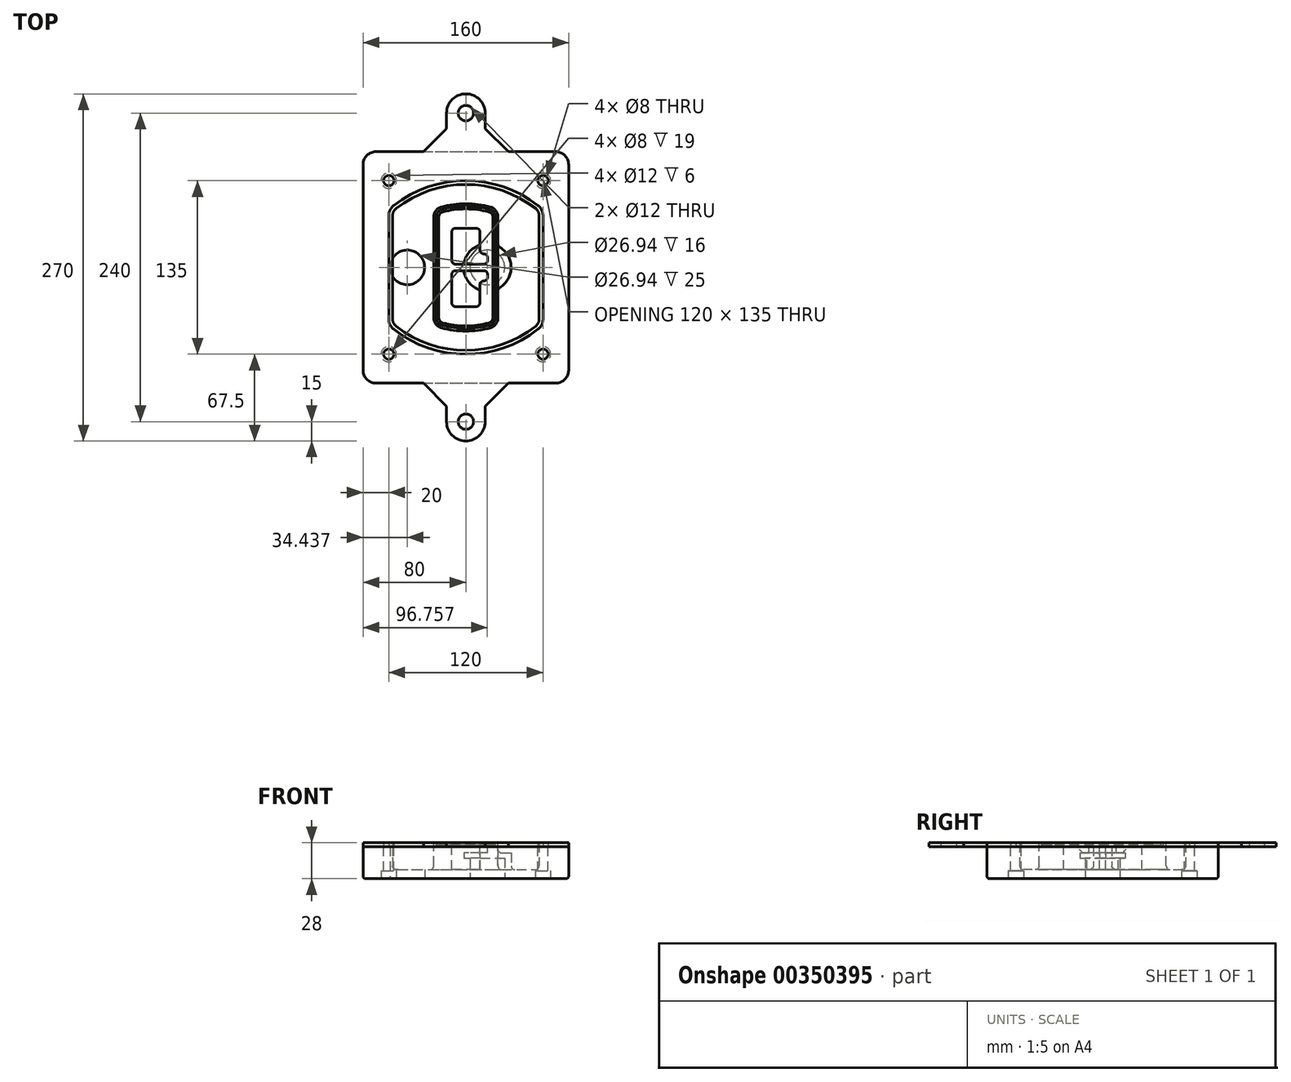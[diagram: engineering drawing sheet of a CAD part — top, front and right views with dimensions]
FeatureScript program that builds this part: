
annotation { "Feature Type Name" : "Feature", "Feature Type Description" : "" }
export const myFeature = defineFeature(function(context is Context, id is Id, definition is map)
    precondition{}
    {
        {
            var Q0;
            Q0=qCreatedBy(makeId("Top.planeOp"),FACE);
            var sketch = newSketch(context, id + "F0", { "sketchPlane" : qUnion([Q0])});
            skPoint(sketch, "E0.rect.middle", {"position": v(0, 0) * mm});
            skLineSegment(sketch, "E1.bottom", {"start": v(-70, -90) * mm, "end": v(70, -90) * mm});
            skLineSegment(sketch, "E1.top", {"start": v(-70, 90) * mm, "end": v(70, 90) * mm});
            skLineSegment(sketch, "E1.left", {"start": v(-80, -80) * mm, "end": v(-80, 80) * mm});
            skLineSegment(sketch, "E1.right", {"start": v(80, -80) * mm, "end": v(80, 80) * mm});
            skLineSegment(sketch, "E2", {"start": v(-80, 90) * mm, "end": v(80, -90) * mm, "construction": true});
            skLineSegment(sketch, "E3", {"start": v(80, 90) * mm, "end": v(-80, -90) * mm, "construction": true});
            skCircle(sketch, "E4", {"center": v(-60, 67.5) * mm, "radius": 4 * mm});
            skCircle(sketch, "E5", {"center": v(60, 67.5) * mm, "radius": 4 * mm});
            skCircle(sketch, "E6", {"center": v(60, -67.5) * mm, "radius": 4 * mm});
            skCircle(sketch, "E7", {"center": v(-60, -67.5) * mm, "radius": 4 * mm});
            skLineSegment(sketch, "E8", {"start": v(-60, 67.5) * mm, "end": v(60, 67.5) * mm, "construction": true});
            skLineSegment(sketch, "E9", {"start": v(60, 67.5) * mm, "end": v(60, -67.5) * mm, "construction": true});
            skLineSegment(sketch, "E10", {"start": v(60, -67.5) * mm, "end": v(-60, -67.5) * mm, "construction": true});
            skLineSegment(sketch, "E11", {"start": v(-60, -67.5) * mm, "end": v(-60, 67.5) * mm, "construction": true});
            skLineSegment(sketch, "E12", {"start": v(-60, 40.3) * mm, "end": v(-60, -40.3) * mm});
            skLineSegment(sketch, "E13", {"start": v(60, 40.3) * mm, "end": v(60, -40.3) * mm});
            skArc(sketch, "E14", {"start": v(56.15, 48.18) * mm, "mid": v(0, 67.5) * mm, "end": v(-56.15, 48.18) * mm});
            skArc(sketch, "E15", {"start": v(-56.15, -48.18) * mm, "mid": v(0, -67.5) * mm, "end": v(56.15, -48.18) * mm});
            skLineSegment(sketch, "E16", {"start": v(-60, 0) * mm, "end": v(60, 0) * mm, "construction": true});
            skPoint(sketch, "E17.visualSharp", {"position": v(-60, -45) * mm});
            skArc(sketch, "E17.filletArc", {"start": v(-60, -40.3) * mm, "mid": v(-58.99, -44.68) * mm, "end": v(-56.15, -48.18) * mm});
            skPoint(sketch, "E18.visualSharp", {"position": v(-60, 45) * mm});
            skArc(sketch, "E18.filletArc", {"start": v(-56.15, 48.18) * mm, "mid": v(-58.99, 44.68) * mm, "end": v(-60, 40.3) * mm});
            skPoint(sketch, "E19.visualSharp", {"position": v(60, 45) * mm});
            skArc(sketch, "E19.filletArc", {"start": v(60, 40.3) * mm, "mid": v(58.99, 44.68) * mm, "end": v(56.15, 48.18) * mm});
            skPoint(sketch, "E20.visualSharp", {"position": v(60, -45) * mm});
            skArc(sketch, "E20.filletArc", {"start": v(56.15, -48.18) * mm, "mid": v(58.99, -44.68) * mm, "end": v(60, -40.3) * mm});
            skPoint(sketch, "E21.visualSharp", {"position": v(-80, 90) * mm});
            skArc(sketch, "E21.filletArc", {"start": v(-70, 90) * mm, "mid": v(-77.07, 87.07) * mm, "end": v(-80, 80) * mm});
            skPoint(sketch, "E22.visualSharp", {"position": v(80, 90) * mm});
            skArc(sketch, "E22.filletArc", {"start": v(80, 80) * mm, "mid": v(77.07, 87.07) * mm, "end": v(70, 90) * mm});
            skPoint(sketch, "E23.visualSharp", {"position": v(80, -90) * mm});
            skArc(sketch, "E23.filletArc", {"start": v(70, -90) * mm, "mid": v(77.07, -87.07) * mm, "end": v(80, -80) * mm});
            skPoint(sketch, "E24.visualSharp", {"position": v(-80, -90) * mm});
            skArc(sketch, "E24.filletArc", {"start": v(-80, -80) * mm, "mid": v(-77.07, -87.07) * mm, "end": v(-70, -90) * mm});
            skArc(sketch, "E25.0", {"start": v(57, 40.3) * mm, "mid": v(56.3, 43.36) * mm, "end": v(54.3, 45.81) * mm});
            skLineSegment(sketch, "E25.1", {"start": v(57, 40.3) * mm, "end": v(57, -40.3) * mm});
            skArc(sketch, "E25.2", {"start": v(54.3, -45.81) * mm, "mid": v(56.3, -43.36) * mm, "end": v(57, -40.3) * mm});
            skArc(sketch, "E25.3", {"start": v(-54.3, -45.81) * mm, "mid": v(0, -64.5) * mm, "end": v(54.3, -45.81) * mm});
            skArc(sketch, "E25.4", {"start": v(-57, -40.3) * mm, "mid": v(-56.3, -43.36) * mm, "end": v(-54.3, -45.81) * mm});
            skArc(sketch, "E25.5", {"start": v(54.3, 45.81) * mm, "mid": v(0, 64.5) * mm, "end": v(-54.3, 45.81) * mm});
            skLineSegment(sketch, "E25.6", {"start": v(-57, 40.3) * mm, "end": v(-57, -40.3) * mm});
            skArc(sketch, "E25.7", {"start": v(-54.3, 45.81) * mm, "mid": v(-56.3, 43.36) * mm, "end": v(-57, 40.3) * mm});
            skArc(sketch, "E26.0", {"start": v(-58.62, 51.33) * mm, "mid": v(-62.58, 46.43) * mm, "end": v(-64, 40.3) * mm});
            skArc(sketch, "E26.1", {"start": v(58.62, 51.33) * mm, "mid": v(0, 71.5) * mm, "end": v(-58.62, 51.33) * mm});
            skArc(sketch, "E26.2", {"start": v(64, 40.3) * mm, "mid": v(62.58, 46.43) * mm, "end": v(58.62, 51.33) * mm});
            skLineSegment(sketch, "E26.3", {"start": v(64, 40.3) * mm, "end": v(64, -40.3) * mm});
            skArc(sketch, "E26.4", {"start": v(58.62, -51.33) * mm, "mid": v(62.58, -46.43) * mm, "end": v(64, -40.3) * mm});
            skLineSegment(sketch, "E26.5", {"start": v(-64, 40.3) * mm, "end": v(-64, -40.3) * mm});
            skArc(sketch, "E26.6", {"start": v(-58.62, -51.33) * mm, "mid": v(0, -71.5) * mm, "end": v(58.62, -51.33) * mm});
            skArc(sketch, "E26.7", {"start": v(-64, -40.3) * mm, "mid": v(-62.58, -46.43) * mm, "end": v(-58.62, -51.33) * mm});
            skSolve(sketch);
        }
        {
            var Q0;
            Q0=makeQuery(id+"F0.imprint","IMPRINT",FACE,{"disambiguationData":[TD([[makeQuery(id+"F0.imprint","IMPRINT",EDGE,{"derivedFrom":sQuery(id+"F0.wireOp",EDGE,"E1.bottom")}),1.0]])]});
            var Q1;
            Q1=makeQuery(id+"F0.imprint","IMPRINT",FACE,{"disambiguationData":[TD([[makeQuery(id+"F0.imprint","IMPRINT",EDGE,{"derivedFrom":sQuery(id+"F0.wireOp",EDGE,"E12")}),1.0]])]});
            var Q2;
            Q2=makeQuery(id+"F0.imprint","IMPRINT",FACE,{"disambiguationData":[TD([[makeQuery(id+"F0.imprint","IMPRINT",EDGE,{"derivedFrom":sQuery(id+"F0.wireOp",EDGE,"E25.0")}),1.0]])]});
            var Q3;
            Q3=makeQuery(id+"F0.imprint","IMPRINT",FACE,{"disambiguationData":[TD([[makeQuery(id+"F0.imprint","IMPRINT",EDGE,{"derivedFrom":sQuery(id+"F0.wireOp",EDGE,"E12")}),-1.0]])]});
            extrude(context, id + "F1", {"entities" : qUnion([Q0, Q1, Q2, Q3]), "oppositeDirection" : true, "depth" : 25 * mm});
        }
        {
            var Q0;
            Q0=makeQuery(id+"F0.imprint","IMPRINT",FACE,{"disambiguationData":[TD([[makeQuery(id+"F0.imprint","IMPRINT",EDGE,{"derivedFrom":sQuery(id+"F0.wireOp",EDGE,"E12")}),1.0]])]});
            extrude(context, id + "F2", {"entities" : qUnion([Q0]), "operationType" : NewBodyOperationType.ADD, "depth" : 3 * mm});
        }
        {
            var Q0;
            Q0=makeQuery(id+"F0.imprint","IMPRINT",FACE,{"disambiguationData":[TD([[makeQuery(id+"F0.imprint","IMPRINT",EDGE,{"derivedFrom":sQuery(id+"F0.wireOp",EDGE,"E25.0")}),1.0]])]});
            extrude(context, id + "F3", {"entities" : qUnion([Q0]), "operationType" : NewBodyOperationType.REMOVE, "oppositeDirection" : true, "depth" : 18 * mm});
        }
        {
            var Q0;
            Q0=makeQuery(id+"F2.opExtrude","CAP_FACE",FACE,{"disambiguationData":[OSD([sQuery(id+"F0.wireOp",EDGE,"E12"),sQuery(id+"F0.wireOp",EDGE,"E13"),sQuery(id+"F0.wireOp",EDGE,"E14"),sQuery(id+"F0.wireOp",EDGE,"E15"),sQuery(id+"F0.wireOp",EDGE,"E17.filletArc"),sQuery(id+"F0.wireOp",EDGE,"E18.filletArc"),sQuery(id+"F0.wireOp",EDGE,"E19.filletArc"),sQuery(id+"F0.wireOp",EDGE,"E20.filletArc"),sQuery(id+"F0.wireOp",EDGE,"E25.0"),sQuery(id+"F0.wireOp",EDGE,"E25.1"),sQuery(id+"F0.wireOp",EDGE,"E25.2"),sQuery(id+"F0.wireOp",EDGE,"E25.3"),sQuery(id+"F0.wireOp",EDGE,"E25.4"),sQuery(id+"F0.wireOp",EDGE,"E25.5"),sQuery(id+"F0.wireOp",EDGE,"E25.6"),sQuery(id+"F0.wireOp",EDGE,"E25.7")])],"isStart":false});
            var sketch = newSketch(context, id + "F4", { "sketchPlane" : qUnion([Q0])});
            skArc(sketch, "E27.0", {"start": v(-19.08, -46.97) * mm, "mid": v(0, -49.5) * mm, "end": v(19.08, -46.97) * mm});
            skArc(sketch, "E28.0", {"start": v(19.08, 46.97) * mm, "mid": v(0, 49.5) * mm, "end": v(-19.08, 46.97) * mm});
            skLineSegment(sketch, "E29", {"start": v(-25, 39.25) * mm, "end": v(-25, -39.25) * mm});
            skLineSegment(sketch, "E30", {"start": v(25, 39.25) * mm, "end": v(25, -39.25) * mm});
            skLineSegment(sketch, "E31", {"start": v(-25, 45.1) * mm, "end": v(25, 45.1) * mm, "construction": true});
            skLineSegment(sketch, "E32", {"start": v(-25, -45.1) * mm, "end": v(25, -45.1) * mm, "construction": true});
            skPoint(sketch, "E33.visualSharp", {"position": v(-25, 45.1) * mm});
            skArc(sketch, "E33.filletArc", {"start": v(-19.08, 46.97) * mm, "mid": v(-23.35, 44.11) * mm, "end": v(-25, 39.25) * mm});
            skPoint(sketch, "E34.visualSharp", {"position": v(25, 45.1) * mm});
            skArc(sketch, "E34.filletArc", {"start": v(25, 39.25) * mm, "mid": v(23.35, 44.11) * mm, "end": v(19.08, 46.97) * mm});
            skPoint(sketch, "E35.visualSharp", {"position": v(25, -45.1) * mm});
            skArc(sketch, "E35.filletArc", {"start": v(19.08, -46.97) * mm, "mid": v(23.35, -44.11) * mm, "end": v(25, -39.25) * mm});
            skPoint(sketch, "E36.visualSharp", {"position": v(-25, -45.1) * mm});
            skArc(sketch, "E36.filletArc", {"start": v(-25, -39.25) * mm, "mid": v(-23.35, -44.11) * mm, "end": v(-19.08, -46.97) * mm});
            skArc(sketch, "E37.0", {"start": v(54.3, 45.81) * mm, "mid": v(0, 64.5) * mm, "end": v(-54.3, 45.81) * mm});
            skArc(sketch, "E37.1", {"start": v(-54.3, 45.81) * mm, "mid": v(-56.3, 43.36) * mm, "end": v(-57, 40.3) * mm});
            skLineSegment(sketch, "E37.2", {"start": v(-57, 40.3) * mm, "end": v(-57, -40.3) * mm});
            skArc(sketch, "E37.3", {"start": v(-57, -40.3) * mm, "mid": v(-56.3, -43.36) * mm, "end": v(-54.3, -45.81) * mm});
            skArc(sketch, "E37.4", {"start": v(-54.3, -45.81) * mm, "mid": v(0, -64.5) * mm, "end": v(54.3, -45.81) * mm});
            skArc(sketch, "E37.5", {"start": v(54.3, -45.81) * mm, "mid": v(56.3, -43.36) * mm, "end": v(57, -40.3) * mm});
            skLineSegment(sketch, "E37.6", {"start": v(57, 40.3) * mm, "end": v(57, -40.3) * mm});
            skArc(sketch, "E37.7", {"start": v(57, 40.3) * mm, "mid": v(56.3, 43.36) * mm, "end": v(54.3, 45.81) * mm});
            skLineSegment(sketch, "E38.0", {"start": v(23, 39.25) * mm, "end": v(23, -39.25) * mm});
            skArc(sketch, "E38.1", {"start": v(18.56, -45.04) * mm, "mid": v(21.76, -42.9) * mm, "end": v(23, -39.25) * mm});
            skArc(sketch, "E38.2", {"start": v(-18.56, -45.04) * mm, "mid": v(0, -47.5) * mm, "end": v(18.56, -45.04) * mm});
            skArc(sketch, "E38.3", {"start": v(-23, -39.25) * mm, "mid": v(-21.76, -42.9) * mm, "end": v(-18.56, -45.04) * mm});
            skLineSegment(sketch, "E38.4", {"start": v(-23, 39.25) * mm, "end": v(-23, -39.25) * mm});
            skArc(sketch, "E38.5", {"start": v(23, 39.25) * mm, "mid": v(21.76, 42.9) * mm, "end": v(18.56, 45.04) * mm});
            skArc(sketch, "E38.6", {"start": v(-18.56, 45.04) * mm, "mid": v(-21.76, 42.9) * mm, "end": v(-23, 39.25) * mm});
            skArc(sketch, "E38.7", {"start": v(18.56, 45.04) * mm, "mid": v(0, 47.5) * mm, "end": v(-18.56, 45.04) * mm});
            skArc(sketch, "E39.0", {"start": v(21, 39.25) * mm, "mid": v(20.18, 41.68) * mm, "end": v(18.04, 43.1) * mm});
            skLineSegment(sketch, "E39.1", {"start": v(21, 39.25) * mm, "end": v(21, -39.25) * mm});
            skArc(sketch, "E39.2", {"start": v(18.04, -43.1) * mm, "mid": v(20.18, -41.68) * mm, "end": v(21, -39.25) * mm});
            skArc(sketch, "E39.3", {"start": v(-18.04, -43.1) * mm, "mid": v(0, -45.5) * mm, "end": v(18.04, -43.1) * mm});
            skArc(sketch, "E39.4", {"start": v(-21, -39.25) * mm, "mid": v(-20.18, -41.68) * mm, "end": v(-18.04, -43.1) * mm});
            skArc(sketch, "E39.5", {"start": v(18.04, 43.1) * mm, "mid": v(0, 45.5) * mm, "end": v(-18.04, 43.1) * mm});
            skLineSegment(sketch, "E39.6", {"start": v(-21, 39.25) * mm, "end": v(-21, -39.25) * mm});
            skArc(sketch, "E39.7", {"start": v(-18.04, 43.1) * mm, "mid": v(-20.18, 41.68) * mm, "end": v(-21, 39.25) * mm});
            skLineSegment(sketch, "E40", {"start": v(-25, 0) * mm, "end": v(25, 0) * mm, "construction": true});
            skLineSegment(sketch, "E41", {"start": v(-11, 5.5) * mm, "end": v(-11, 27.5) * mm});
            skLineSegment(sketch, "E42", {"start": v(-8, 30.5) * mm, "end": v(8, 30.5) * mm});
            skLineSegment(sketch, "E43", {"start": v(11, 27.5) * mm, "end": v(11, 13.5) * mm});
            skLineSegment(sketch, "E44", {"start": v(14, 10.5) * mm, "end": v(14, 10.5) * mm});
            skLineSegment(sketch, "E45", {"start": v(17, 7.5) * mm, "end": v(17, 5.5) * mm});
            skLineSegment(sketch, "E46", {"start": v(14, 2.5) * mm, "end": v(-8, 2.5) * mm});
            skPoint(sketch, "E47.visualSharp", {"position": v(-11, 30.5) * mm});
            skArc(sketch, "E47.filletArc", {"start": v(-8, 30.5) * mm, "mid": v(-10.12, 29.62) * mm, "end": v(-11, 27.5) * mm});
            skPoint(sketch, "E48.visualSharp", {"position": v(11, 30.5) * mm});
            skArc(sketch, "E48.filletArc", {"start": v(11, 27.5) * mm, "mid": v(10.12, 29.62) * mm, "end": v(8, 30.5) * mm});
            skPoint(sketch, "E49.visualSharp", {"position": v(11, 10.5) * mm});
            skArc(sketch, "E49.filletArc", {"start": v(11, 13.5) * mm, "mid": v(11.88, 11.38) * mm, "end": v(14, 10.5) * mm});
            skPoint(sketch, "E50.visualSharp", {"position": v(17, 10.5) * mm});
            skArc(sketch, "E50.filletArc", {"start": v(17, 7.5) * mm, "mid": v(16.12, 9.62) * mm, "end": v(14, 10.5) * mm});
            skPoint(sketch, "E51.visualSharp", {"position": v(17, 2.5) * mm});
            skArc(sketch, "E51.filletArc", {"start": v(14, 2.5) * mm, "mid": v(16.12, 3.38) * mm, "end": v(17, 5.5) * mm});
            skPoint(sketch, "E52.visualSharp", {"position": v(-11, 2.5) * mm});
            skArc(sketch, "E52.filletArc", {"start": v(-11, 5.5) * mm, "mid": v(-10.12, 3.38) * mm, "end": v(-8, 2.5) * mm});
            skLineSegment(sketch, "E53.0.MirrorCS", {"start": v(14, -2.5) * mm, "end": v(-8, -2.5) * mm});
            skArc(sketch, "E54.0.MirrorCS", {"start": v(-11, -5.5) * mm, "mid": v(-10.12, -3.38) * mm, "end": v(-8, -2.5) * mm});
            skLineSegment(sketch, "E55.0.MirrorCS", {"start": v(-11, -5.5) * mm, "end": v(-11, -27.5) * mm});
            skArc(sketch, "E56.0.MirrorCS", {"start": v(-8, -30.5) * mm, "mid": v(-10.12, -29.62) * mm, "end": v(-11, -27.5) * mm});
            skLineSegment(sketch, "E57.0.MirrorCS", {"start": v(-8, -30.5) * mm, "end": v(8, -30.5) * mm});
            skArc(sketch, "E58.0.MirrorCS", {"start": v(11, -27.5) * mm, "mid": v(10.12, -29.62) * mm, "end": v(8, -30.5) * mm});
            skLineSegment(sketch, "E59.0.MirrorCS", {"start": v(11, -27.5) * mm, "end": v(11, -13.5) * mm});
            skArc(sketch, "E60.0.MirrorCS", {"start": v(11, -13.5) * mm, "mid": v(11.88, -11.38) * mm, "end": v(14, -10.5) * mm});
            skArc(sketch, "E61.0.MirrorCS", {"start": v(17, -7.5) * mm, "mid": v(16.12, -9.62) * mm, "end": v(14, -10.5) * mm});
            skLineSegment(sketch, "E62.0.MirrorCS", {"start": v(17, -7.5) * mm, "end": v(17, -5.5) * mm});
            skArc(sketch, "E63.0.MirrorCS", {"start": v(14, -2.5) * mm, "mid": v(16.12, -3.38) * mm, "end": v(17, -5.5) * mm});
            skSolve(sketch);
        }
        {
            var Q0;
            Q0=makeQuery(id+"F4.imprint","IMPRINT",FACE,{"disambiguationData":[TD([[makeQuery(id+"F4.imprint","IMPRINT",EDGE,{"derivedFrom":sQuery(id+"F4.wireOp",EDGE,"E27.0")}),1.0]])]});
            var Q1;
            Q1=makeQuery(id+"F4.imprint","IMPRINT",FACE,{"disambiguationData":[TD([[makeQuery(id+"F4.imprint","IMPRINT",EDGE,{"derivedFrom":sQuery(id+"F4.wireOp",EDGE,"E38.0")}),-1.0]])]});
            var Q2;
            Q2=makeQuery(id+"F4.imprint","IMPRINT",FACE,{"disambiguationData":[TD([[makeQuery(id+"F4.imprint","IMPRINT",EDGE,{"derivedFrom":sQuery(id+"F4.wireOp",EDGE,"E39.0")}),1.0]])]});
            extrude(context, id + "F5", {"entities" : qUnion([Q0, Q1, Q2]), "operationType" : NewBodyOperationType.ADD, "endBound" : BoundingType.UP_TO_NEXT, "oppositeDirection" : true, "depth" : 25 * mm});
        }
        {
            var Q0;
            Q0=makeQuery(id+"F4.imprint","IMPRINT",FACE,{"disambiguationData":[TD([[makeQuery(id+"F4.imprint","IMPRINT",EDGE,{"derivedFrom":sQuery(id+"F4.wireOp",EDGE,"E38.0")}),-1.0]])]});
            extrude(context, id + "F6", {"entities" : qUnion([Q0]), "operationType" : NewBodyOperationType.REMOVE, "oppositeDirection" : true, "depth" : 2 * mm});
        }
        {
            var Q0;
            Q0=makeQuery(id+"F1.opExtrude","CAP_FACE",FACE,{"disambiguationData":[OSD([sQuery(id+"F0.wireOp",EDGE,"E1.bottom"),sQuery(id+"F0.wireOp",EDGE,"E1.top"),sQuery(id+"F0.wireOp",EDGE,"E1.left"),sQuery(id+"F0.wireOp",EDGE,"E1.right"),sQuery(id+"F0.wireOp",EDGE,"E4"),sQuery(id+"F0.wireOp",EDGE,"E5"),sQuery(id+"F0.wireOp",EDGE,"E6"),sQuery(id+"F0.wireOp",EDGE,"E7"),sQuery(id+"F0.wireOp",EDGE,"E21.filletArc"),sQuery(id+"F0.wireOp",EDGE,"E22.filletArc"),sQuery(id+"F0.wireOp",EDGE,"E23.filletArc"),sQuery(id+"F0.wireOp",EDGE,"E24.filletArc")])],"isStart":false});
            var sketch = newSketch(context, id + "F7", { "sketchPlane" : qUnion([Q0])});
            skCircle(sketch, "E64", {"center": v(16.76, 0) * mm, "radius": 13.47 * mm});
            skCircle(sketch, "E65", {"center": v(-45.56, 0) * mm, "radius": 13.47 * mm});
            skLineSegment(sketch, "E66", {"start": v(80, 0) * mm, "end": v(-80, 0) * mm});
            skCircle(sketch, "E67", {"center": v(16.76, 0) * mm, "radius": 18.47 * mm});
            skCircle(sketch, "E68", {"center": v(60, -67.5) * mm, "radius": 6 * mm});
            skCircle(sketch, "E69", {"center": v(-60, -67.5) * mm, "radius": 6 * mm});
            skCircle(sketch, "E70", {"center": v(-60, 67.5) * mm, "radius": 6 * mm});
            skCircle(sketch, "E71", {"center": v(60, 67.5) * mm, "radius": 6 * mm});
            skSolve(sketch);
        }
        {
            var Q0;
            {var subQ1=sQuery(id+"F7.wireOp",EDGE,"E66");var subQ4=sQuery(id+"F7.wireOp",EDGE,"E64");var subQ6=makeQuery(id+"F7.imprint","INTERSECT",VERTEX,{"disambiguationData":[OD(0.0)],"derivedFrom":[subQ4,subQ1]});Q0=makeQuery(id+"F7.imprint","IMPRINT",FACE,{"disambiguationData":[TD([[makeQuery(id+"F7.imprint","IMPRINT",EDGE,{"disambiguationData":[TD([[subQ6,-1.0]])],"derivedFrom":subQ4}),-1.0]])]});}
            var Q1;
            {var subQ0=sQuery(id+"F7.wireOp",EDGE,"E66");var subQ1=sQuery(id+"F7.wireOp",EDGE,"E64");var subQ3=makeQuery(id+"F7.imprint","INTERSECT",VERTEX,{"disambiguationData":[OD(0.0)],"derivedFrom":[subQ1,subQ0]});Q1=makeQuery(id+"F7.imprint","IMPRINT",FACE,{"disambiguationData":[TD([[makeQuery(id+"F7.imprint","IMPRINT",EDGE,{"disambiguationData":[TD([[subQ3,-1.0]])],"derivedFrom":subQ1}),1.0]])]});}
            var Q2;
            {var subQ0=sQuery(id+"F7.wireOp",EDGE,"E66");var subQ1=sQuery(id+"F7.wireOp",EDGE,"E64");var subQ3=makeQuery(id+"F7.imprint","INTERSECT",VERTEX,{"disambiguationData":[OD(0.0)],"derivedFrom":[subQ1,subQ0]});Q2=makeQuery(id+"F7.imprint","IMPRINT",FACE,{"disambiguationData":[TD([[makeQuery(id+"F7.imprint","IMPRINT",EDGE,{"disambiguationData":[TD([[subQ3,1.0]])],"derivedFrom":subQ1}),1.0]])]});}
            var Q3;
            {var subQ1=sQuery(id+"F7.wireOp",EDGE,"E66");var subQ4=sQuery(id+"F7.wireOp",EDGE,"E64");var subQ6=makeQuery(id+"F7.imprint","INTERSECT",VERTEX,{"disambiguationData":[OD(0.0)],"derivedFrom":[subQ4,subQ1]});Q3=makeQuery(id+"F7.imprint","IMPRINT",FACE,{"disambiguationData":[TD([[makeQuery(id+"F7.imprint","IMPRINT",EDGE,{"disambiguationData":[TD([[subQ6,1.0]])],"derivedFrom":subQ4}),-1.0]])]});}
            extrude(context, id + "F8", {"entities" : qUnion([Q0, Q1, Q2, Q3]), "operationType" : NewBodyOperationType.ADD, "oppositeDirection" : true, "depth" : 20 * mm});
        }
        {
            var Q0;
            {var subQ0=sQuery(id+"F7.wireOp",EDGE,"E66");var subQ1=sQuery(id+"F7.wireOp",EDGE,"E64");var subQ3=makeQuery(id+"F7.imprint","INTERSECT",VERTEX,{"disambiguationData":[OD(0.0)],"derivedFrom":[subQ1,subQ0]});Q0=makeQuery(id+"F7.imprint","IMPRINT",FACE,{"disambiguationData":[TD([[makeQuery(id+"F7.imprint","IMPRINT",EDGE,{"disambiguationData":[TD([[subQ3,-1.0]])],"derivedFrom":subQ1}),1.0]])]});}
            var Q1;
            {var subQ0=sQuery(id+"F7.wireOp",EDGE,"E66");var subQ1=sQuery(id+"F7.wireOp",EDGE,"E64");var subQ3=makeQuery(id+"F7.imprint","INTERSECT",VERTEX,{"disambiguationData":[OD(0.0)],"derivedFrom":[subQ1,subQ0]});Q1=makeQuery(id+"F7.imprint","IMPRINT",FACE,{"disambiguationData":[TD([[makeQuery(id+"F7.imprint","IMPRINT",EDGE,{"disambiguationData":[TD([[subQ3,1.0]])],"derivedFrom":subQ1}),1.0]])]});}
            extrude(context, id + "F9", {"entities" : qUnion([Q0, Q1]), "operationType" : NewBodyOperationType.REMOVE, "oppositeDirection" : true, "depth" : 16 * mm});
        }
        {
            var Q0;
            {var subQ0=sQuery(id+"F7.wireOp",EDGE,"E66");var subQ1=sQuery(id+"F7.wireOp",EDGE,"E65");var subQ3=makeQuery(id+"F7.imprint","INTERSECT",VERTEX,{"disambiguationData":[OD(0.0)],"derivedFrom":[subQ1,subQ0]});Q0=makeQuery(id+"F7.imprint","IMPRINT",FACE,{"disambiguationData":[TD([[makeQuery(id+"F7.imprint","IMPRINT",EDGE,{"disambiguationData":[TD([[subQ3,-1.0]])],"derivedFrom":subQ1}),1.0]])]});}
            var Q1;
            {var subQ0=sQuery(id+"F7.wireOp",EDGE,"E66");var subQ1=sQuery(id+"F7.wireOp",EDGE,"E65");var subQ3=makeQuery(id+"F7.imprint","INTERSECT",VERTEX,{"disambiguationData":[OD(0.0)],"derivedFrom":[subQ1,subQ0]});Q1=makeQuery(id+"F7.imprint","IMPRINT",FACE,{"disambiguationData":[TD([[makeQuery(id+"F7.imprint","IMPRINT",EDGE,{"disambiguationData":[TD([[subQ3,1.0]])],"derivedFrom":subQ1}),1.0]])]});}
            extrude(context, id + "F10", {"entities" : qUnion([Q0, Q1]), "operationType" : NewBodyOperationType.REMOVE, "oppositeDirection" : true, "depth" : 25 * mm});
        }
        {
            var Q0;
            Q0=makeQuery(id+"F7.imprint","IMPRINT",FACE,{"disambiguationData":[TD([[makeQuery(id+"F7.imprint","IMPRINT",EDGE,{"derivedFrom":sQuery(id+"F7.wireOp",EDGE,"E68")}),1.0]])]});
            var Q1;
            Q1=makeQuery(id+"F7.imprint","IMPRINT",FACE,{"disambiguationData":[TD([[makeQuery(id+"F7.imprint","IMPRINT",EDGE,{"derivedFrom":makeQuery(id+"F1.opExtrude","CAP_EDGE",EDGE,{"disambiguationData":[OSD([sQuery(id+"F0.wireOp",EDGE,"E5")])],"isStart":false})}),-1.0]])]});
            var Q2;
            Q2=makeQuery(id+"F7.imprint","IMPRINT",FACE,{"disambiguationData":[TD([[makeQuery(id+"F7.imprint","IMPRINT",EDGE,{"derivedFrom":sQuery(id+"F7.wireOp",EDGE,"E69")}),1.0]])]});
            var Q3;
            Q3=makeQuery(id+"F7.imprint","IMPRINT",FACE,{"disambiguationData":[TD([[makeQuery(id+"F7.imprint","IMPRINT",EDGE,{"derivedFrom":makeQuery(id+"F1.opExtrude","CAP_EDGE",EDGE,{"disambiguationData":[OSD([sQuery(id+"F0.wireOp",EDGE,"E4")])],"isStart":false})}),-1.0]])]});
            var Q4;
            Q4=makeQuery(id+"F7.imprint","IMPRINT",FACE,{"disambiguationData":[TD([[makeQuery(id+"F7.imprint","IMPRINT",EDGE,{"derivedFrom":sQuery(id+"F7.wireOp",EDGE,"E70")}),1.0]])]});
            var Q5;
            Q5=makeQuery(id+"F7.imprint","IMPRINT",FACE,{"disambiguationData":[TD([[makeQuery(id+"F7.imprint","IMPRINT",EDGE,{"derivedFrom":makeQuery(id+"F1.opExtrude","CAP_EDGE",EDGE,{"disambiguationData":[OSD([sQuery(id+"F0.wireOp",EDGE,"E7")])],"isStart":false})}),-1.0]])]});
            var Q6;
            Q6=makeQuery(id+"F7.imprint","IMPRINT",FACE,{"disambiguationData":[TD([[makeQuery(id+"F7.imprint","IMPRINT",EDGE,{"derivedFrom":sQuery(id+"F7.wireOp",EDGE,"E71")}),1.0]])]});
            var Q7;
            Q7=makeQuery(id+"F7.imprint","IMPRINT",FACE,{"disambiguationData":[TD([[makeQuery(id+"F7.imprint","IMPRINT",EDGE,{"derivedFrom":makeQuery(id+"F1.opExtrude","CAP_EDGE",EDGE,{"disambiguationData":[OSD([sQuery(id+"F0.wireOp",EDGE,"E6")])],"isStart":false})}),-1.0]])]});
            extrude(context, id + "F11", {"entities" : qUnion([Q0, Q1, Q2, Q3, Q4, Q5, Q6, Q7]), "operationType" : NewBodyOperationType.REMOVE, "oppositeDirection" : true, "depth" : 6 * mm});
        }
        {
            var Q0;
            Q0=makeQuery(id+"F9.boolean.opBoolean","COPY",FACE,{"derivedFrom":makeQuery(id+"F9.opExtrude","CAP_FACE",FACE,{"disambiguationData":[OSD([sQuery(id+"F7.wireOp",EDGE,"E64")])],"isStart":false})});
            var sketch = newSketch(context, id + "F12", { "sketchPlane" : qUnion([Q0])});
            skArc(sketch, "E72.0", {"start": v(11, 17.55) * mm, "mid": v(2.57, 11.82) * mm, "end": v(-1.54, 2.5) * mm});
            skArc(sketch, "E72.1", {"start": v(-1.54, -2.5) * mm, "mid": v(2.57, -11.82) * mm, "end": v(11, -17.55) * mm});
            skLineSegment(sketch, "E73", {"start": v(-1.54, -2.5) * mm, "end": v(14, -2.5) * mm});
            skLineSegment(sketch, "E74.0", {"start": v(14, 2.5) * mm, "end": v(-1.54, 2.5) * mm});
            skArc(sketch, "E74.1", {"start": v(14, 2.5) * mm, "mid": v(16.12, 3.38) * mm, "end": v(17, 5.5) * mm});
            skLineSegment(sketch, "E74.2", {"start": v(17, 7.5) * mm, "end": v(17, 5.5) * mm});
            skArc(sketch, "E74.3", {"start": v(17, 7.5) * mm, "mid": v(16.12, 9.62) * mm, "end": v(14, 10.5) * mm});
            skArc(sketch, "E74.4", {"start": v(11, 13.5) * mm, "mid": v(11.88, 11.38) * mm, "end": v(14, 10.5) * mm});
            skLineSegment(sketch, "E74.5", {"start": v(11, 17.55) * mm, "end": v(11, 13.5) * mm});
            skLineSegment(sketch, "E74.7", {"start": v(14, -2.5) * mm, "end": v(-1.54, -2.5) * mm});
            skArc(sketch, "E74.8", {"start": v(14, -2.5) * mm, "mid": v(16.12, -3.38) * mm, "end": v(17, -5.5) * mm});
            skLineSegment(sketch, "E74.9", {"start": v(17, -7.5) * mm, "end": v(17, -5.5) * mm});
            skArc(sketch, "E74.10", {"start": v(17, -7.5) * mm, "mid": v(16.12, -9.62) * mm, "end": v(14, -10.5) * mm});
            skArc(sketch, "E74.11", {"start": v(11, -13.5) * mm, "mid": v(11.88, -11.38) * mm, "end": v(14, -10.5) * mm});
            skLineSegment(sketch, "E74.12", {"start": v(11, -17.55) * mm, "end": v(11, -13.5) * mm});
            skPoint(sketch, "E75.orphan", {"position": v(11, -27.5) * mm});
            skPoint(sketch, "E76.orphan", {"position": v(-8, -2.5) * mm});
            skPoint(sketch, "E77.orphan", {"position": v(-8, 2.5) * mm});
            skPoint(sketch, "E78.orphan", {"position": v(11, 27.5) * mm});
            skSolve(sketch);
        }
        {
            var Q0;
            {var subQ7=sQuery(id+"F12.wireOp",EDGE,"E72.0");var subQ14=sQuery(id+"F12.wireOp",EDGE,"E72.1");var subQ16=sQuery(id+"F12.wireOp",EDGE,"E74.1");var subQ18=sQuery(id+"F12.wireOp",EDGE,"E74.8");Q0=qUnion([makeQuery(id+"F12.imprint","IMPRINT",FACE,{"disambiguationData":[TD([[makeQuery(id+"F12.imprint","IMPRINT",EDGE,{"derivedFrom":subQ7}),1.0]])]}),makeQuery(id+"F12.imprint","IMPRINT",FACE,{"disambiguationData":[TD([[makeQuery(id+"F12.imprint","IMPRINT",EDGE,{"derivedFrom":subQ14}),1.0]])]}),makeQuery(id+"F12.imprint","IMPRINT",FACE,{"disambiguationData":[TD([[makeQuery(id+"F12.imprint","IMPRINT",EDGE,{"derivedFrom":subQ16}),1.0]])]}),makeQuery(id+"F12.imprint","IMPRINT",FACE,{"disambiguationData":[TD([[makeQuery(id+"F12.imprint","IMPRINT",EDGE,{"derivedFrom":subQ18}),-1.0]])]})]);}
            var Q1;
            Q1=makeQuery(id+"F5.boolean.opBoolean","SPLIT",FACE,{"disambiguationData":[TD([makeQuery(id+"F5.opExtrude","SWEPT_FACE",FACE,{"disambiguationData":[OSD([sQuery(id+"F4.wireOp",EDGE,"E41")])]})])],"derivedFrom":makeQuery(id+"F3.boolean.opBoolean","COPY",FACE,{"derivedFrom":makeQuery(id+"F3.opExtrude","CAP_FACE",FACE,{"disambiguationData":[OSD([sQuery(id+"F0.wireOp",EDGE,"E25.0"),sQuery(id+"F0.wireOp",EDGE,"E25.1"),sQuery(id+"F0.wireOp",EDGE,"E25.2"),sQuery(id+"F0.wireOp",EDGE,"E25.3"),sQuery(id+"F0.wireOp",EDGE,"E25.4"),sQuery(id+"F0.wireOp",EDGE,"E25.5"),sQuery(id+"F0.wireOp",EDGE,"E25.6"),sQuery(id+"F0.wireOp",EDGE,"E25.7")])],"isStart":false})})});
            extrude(context, id + "F13", {"entities" : qUnion([Q0]), "operationType" : NewBodyOperationType.REMOVE, "endBound" : BoundingType.UP_TO_SURFACE, "endBoundEntityFace" : qUnion([Q1]), "depth" : 25 * mm});
        }
        {
            var Q0;
            Q0=makeQuery(id+"F3.boolean.opBoolean","COPY",EDGE,{"derivedFrom":makeQuery(id+"F3.opExtrude","CAP_EDGE",EDGE,{"disambiguationData":[OSD([sQuery(id+"F0.wireOp",EDGE,"E25.6")])],"isStart":false})});
            var Q1;
            Q1=makeQuery(id+"F8.boolean.opBoolean","INTERSECT",EDGE,{"derivedFrom":[makeQuery(id+"F5.opExtrude","SWEPT_FACE",FACE,{"disambiguationData":[OSD([sQuery(id+"F4.wireOp",EDGE,"E30")])]}),makeQuery(id+"F8.opExtrude","CAP_FACE",FACE,{"disambiguationData":[OSD([sQuery(id+"F7.wireOp",EDGE,"E67")])],"isStart":false})]});
            var Q2;
            Q2=makeQuery(id+"F8.boolean.opBoolean","INTERSECT",EDGE,{"disambiguationData":[OD(1.0)],"derivedFrom":[makeQuery(id+"F5.opExtrude","SWEPT_FACE",FACE,{"disambiguationData":[OSD([sQuery(id+"F4.wireOp",EDGE,"E30")])]}),makeQuery(id+"F8.opExtrude","SWEPT_FACE",FACE,{"disambiguationData":[OSD([sQuery(id+"F7.wireOp",EDGE,"E67")])]})]});
            var Q3;
            {var subQ0=sQuery(id+"F4.wireOp",EDGE,"E30");Q3=makeQuery(id+"F8.boolean.opBoolean","SPLIT",EDGE,{"disambiguationData":[TD([makeQuery(id+"F5.opExtrude","SWEPT_FACE",FACE,{"disambiguationData":[OSD([sQuery(id+"F4.wireOp",EDGE,"E35.filletArc")])]})])],"derivedFrom":makeQuery(id+"F5.opExtrude","CAP_EDGE",EDGE,{"disambiguationData":[OSD([subQ0])],"isStart":false})});}
            var Q4;
            {var subQ0=sQuery(id+"F0.wireOp",EDGE,"E25.7");var subQ1=sQuery(id+"F0.wireOp",EDGE,"E25.1");var subQ2=sQuery(id+"F0.wireOp",EDGE,"E25.6");var subQ3=sQuery(id+"F0.wireOp",EDGE,"E25.5");var subQ4=sQuery(id+"F0.wireOp",EDGE,"E25.4");var subQ5=sQuery(id+"F0.wireOp",EDGE,"E25.0");var subQ6=sQuery(id+"F0.wireOp",EDGE,"E25.2");var subQ7=sQuery(id+"F0.wireOp",EDGE,"E25.3");Q4=makeQuery(id+"F8.boolean.opBoolean","INTERSECT",EDGE,{"derivedFrom":[makeQuery(id+"F5.boolean.opBoolean","SPLIT",FACE,{"disambiguationData":[TD([makeQuery(id+"F2.opExtrude","SWEPT_FACE",FACE,{"disambiguationData":[OSD([subQ5])]})])],"derivedFrom":makeQuery(id+"F3.boolean.opBoolean","COPY",FACE,{"derivedFrom":makeQuery(id+"F3.opExtrude","CAP_FACE",FACE,{"disambiguationData":[OSD([subQ5,subQ1,subQ6,subQ7,subQ4,subQ3,subQ2,subQ0])],"isStart":false})})}),makeQuery(id+"F8.opExtrude","SWEPT_FACE",FACE,{"disambiguationData":[OSD([sQuery(id+"F7.wireOp",EDGE,"E67")])]})]});}
            var Q5;
            Q5=makeQuery(id+"F8.boolean.opBoolean","INTERSECT",EDGE,{"disambiguationData":[OD(0.0)],"derivedFrom":[makeQuery(id+"F5.opExtrude","SWEPT_FACE",FACE,{"disambiguationData":[OSD([sQuery(id+"F4.wireOp",EDGE,"E30")])]}),makeQuery(id+"F8.opExtrude","SWEPT_FACE",FACE,{"disambiguationData":[OSD([sQuery(id+"F7.wireOp",EDGE,"E67")])]})]});
            fillet(context, id + "F14", {"entities" : qUnion([Q0, Q1, Q2, Q3, Q4, Q5]), "radius" : 3 * mm, "tangentPropagation" : true, "allowEdgeOverflow" : false});
        }
        {
            var Q0;
            Q0=makeQuery(id+"F1.opExtrude","CAP_EDGE",EDGE,{"disambiguationData":[OSD([sQuery(id+"F0.wireOp",EDGE,"E1.bottom")])],"isStart":false});
            fillet(context, id + "F15", {"entities" : qUnion([Q0]), "radius" : 2 * mm, "tangentPropagation" : true, "allowEdgeOverflow" : false});
        }
        {
            var Q0;
            {var subQ0=sQuery(id+"F0.wireOp",EDGE,"E21.filletArc");var subQ1=sQuery(id+"F0.wireOp",EDGE,"E7");var subQ2=sQuery(id+"F0.wireOp",EDGE,"E6");var subQ3=sQuery(id+"F0.wireOp",EDGE,"E5");var subQ4=sQuery(id+"F0.wireOp",EDGE,"E4");var subQ5=sQuery(id+"F0.wireOp",EDGE,"E22.filletArc");var subQ6=sQuery(id+"F0.wireOp",EDGE,"E1.bottom");var subQ7=sQuery(id+"F0.wireOp",EDGE,"E1.right");var subQ8=sQuery(id+"F0.wireOp",EDGE,"E1.top");var subQ9=sQuery(id+"F0.wireOp",EDGE,"E1.left");var subQ10=sQuery(id+"F0.wireOp",EDGE,"E23.filletArc");var subQ11=sQuery(id+"F0.wireOp",EDGE,"E24.filletArc");Q0=makeQuery(id+"F2.boolean.opBoolean","SPLIT",FACE,{"disambiguationData":[TD([makeQuery(id+"F1.opExtrude","SWEPT_FACE",FACE,{"disambiguationData":[OSD([subQ6])]})])],"derivedFrom":makeQuery(id+"F1.opExtrude","CAP_FACE",FACE,{"disambiguationData":[OSD([subQ6,subQ8,subQ9,subQ7,subQ4,subQ3,subQ2,subQ1,subQ0,subQ5,subQ10,subQ11])],"isStart":true})});}
            var sketch = newSketch(context, id + "F16", { "sketchPlane" : qUnion([Q0])});
            skLineSegment(sketch, "E79.0", {"start": v(-70, 90) * mm, "end": v(70, 90) * mm});
            skArc(sketch, "E79.1", {"start": v(-70, 90) * mm, "mid": v(-77.07, 87.07) * mm, "end": v(-80, 80) * mm});
            skLineSegment(sketch, "E79.2", {"start": v(-80, -80) * mm, "end": v(-80, 80) * mm});
            skArc(sketch, "E79.3", {"start": v(-80, -80) * mm, "mid": v(-77.07, -87.07) * mm, "end": v(-70, -90) * mm});
            skLineSegment(sketch, "E79.4", {"start": v(-70, -90) * mm, "end": v(70, -90) * mm});
            skArc(sketch, "E79.5", {"start": v(70, -90) * mm, "mid": v(77.07, -87.07) * mm, "end": v(80, -80) * mm});
            skLineSegment(sketch, "E79.6", {"start": v(80, -80) * mm, "end": v(80, 80) * mm});
            skArc(sketch, "E79.7", {"start": v(80, 80) * mm, "mid": v(77.07, 87.07) * mm, "end": v(70, 90) * mm});
            skCircle(sketch, "E79.8", {"center": v(-60, -67.5) * mm, "radius": 4 * mm});
            skCircle(sketch, "E79.9", {"center": v(60, -67.5) * mm, "radius": 4 * mm});
            skCircle(sketch, "E79.10", {"center": v(60, 67.5) * mm, "radius": 4 * mm});
            skCircle(sketch, "E79.11", {"center": v(-60, 67.5) * mm, "radius": 4 * mm});
            skArc(sketch, "E79.12", {"start": v(56.15, 48.18) * mm, "mid": v(0, 67.5) * mm, "end": v(-56.15, 48.18) * mm});
            skArc(sketch, "E79.13", {"start": v(-56.15, 48.18) * mm, "mid": v(-58.99, 44.68) * mm, "end": v(-60, 40.3) * mm});
            skLineSegment(sketch, "E79.14", {"start": v(-60, 40.3) * mm, "end": v(-60, -40.3) * mm});
            skArc(sketch, "E79.15", {"start": v(-60, -40.3) * mm, "mid": v(-58.99, -44.68) * mm, "end": v(-56.15, -48.18) * mm});
            skArc(sketch, "E79.16", {"start": v(-56.15, -48.18) * mm, "mid": v(0, -67.5) * mm, "end": v(56.15, -48.18) * mm});
            skArc(sketch, "E79.17", {"start": v(56.15, -48.18) * mm, "mid": v(58.99, -44.68) * mm, "end": v(60, -40.3) * mm});
            skLineSegment(sketch, "E79.18", {"start": v(60, 40.3) * mm, "end": v(60, -40.3) * mm});
            skArc(sketch, "E79.19", {"start": v(60, 40.3) * mm, "mid": v(58.99, 44.68) * mm, "end": v(56.15, 48.18) * mm});
            skLineSegment(sketch, "E80", {"start": v(-80, 0) * mm, "end": v(80, 0) * mm, "construction": true});
            skLineSegment(sketch, "E81", {"start": v(0, 90) * mm, "end": v(0, 120) * mm, "construction": true});
            skCircle(sketch, "E82", {"center": v(0, 120) * mm, "radius": 6 * mm});
            skLineSegment(sketch, "E83", {"start": v(15, 120) * mm, "end": v(15, 108) * mm});
            skLineSegment(sketch, "E84", {"start": v(-15, 120) * mm, "end": v(-15, 108) * mm});
            skLineSegment(sketch, "E85", {"start": v(-15, 108) * mm, "end": v(-33, 90) * mm});
            skLineSegment(sketch, "E86", {"start": v(15, 108) * mm, "end": v(33, 90) * mm});
            skArc(sketch, "E87", {"start": v(15, 120) * mm, "mid": v(0, 135) * mm, "end": v(-15, 120) * mm});
            skLineSegment(sketch, "E88.MirrorCS", {"start": v(0, -90) * mm, "end": v(0, -120) * mm, "construction": true});
            skLineSegment(sketch, "E89.MirrorCS", {"start": v(15, -120) * mm, "end": v(15, -108) * mm});
            skLineSegment(sketch, "E90.MirrorCS", {"start": v(15, -108) * mm, "end": v(33, -90) * mm});
            skLineSegment(sketch, "E91.MirrorCS", {"start": v(-15, -108) * mm, "end": v(-33, -90) * mm});
            skLineSegment(sketch, "E92.MirrorCS", {"start": v(-15, -120) * mm, "end": v(-15, -108) * mm});
            skArc(sketch, "E93.MirrorCS", {"start": v(15, -120) * mm, "mid": v(0, -135) * mm, "end": v(-15, -120) * mm});
            skCircle(sketch, "E94.MirrorC", {"center": v(0, -120) * mm, "radius": 6 * mm});
            skSolve(sketch);
        }
        {
            var Q0;
            Q0 = qSketchRegion(id + "F16", true);
            var Q1;
            Q1=makeQuery(id+"F2.opExtrude","CAP_FACE",FACE,{"disambiguationData":[OSD([sQuery(id+"F0.wireOp",EDGE,"E12"),sQuery(id+"F0.wireOp",EDGE,"E13"),sQuery(id+"F0.wireOp",EDGE,"E14"),sQuery(id+"F0.wireOp",EDGE,"E15"),sQuery(id+"F0.wireOp",EDGE,"E17.filletArc"),sQuery(id+"F0.wireOp",EDGE,"E18.filletArc"),sQuery(id+"F0.wireOp",EDGE,"E19.filletArc"),sQuery(id+"F0.wireOp",EDGE,"E20.filletArc"),sQuery(id+"F0.wireOp",EDGE,"E25.0"),sQuery(id+"F0.wireOp",EDGE,"E25.1"),sQuery(id+"F0.wireOp",EDGE,"E25.2"),sQuery(id+"F0.wireOp",EDGE,"E25.3"),sQuery(id+"F0.wireOp",EDGE,"E25.4"),sQuery(id+"F0.wireOp",EDGE,"E25.5"),sQuery(id+"F0.wireOp",EDGE,"E25.6"),sQuery(id+"F0.wireOp",EDGE,"E25.7")])],"isStart":false});
            extrude(context, id + "F17", {"entities" : qUnion([Q0]), "endBound" : BoundingType.UP_TO_SURFACE, "endBoundEntityFace" : qUnion([Q1]), "depth" : 25 * mm});
        }
    });
